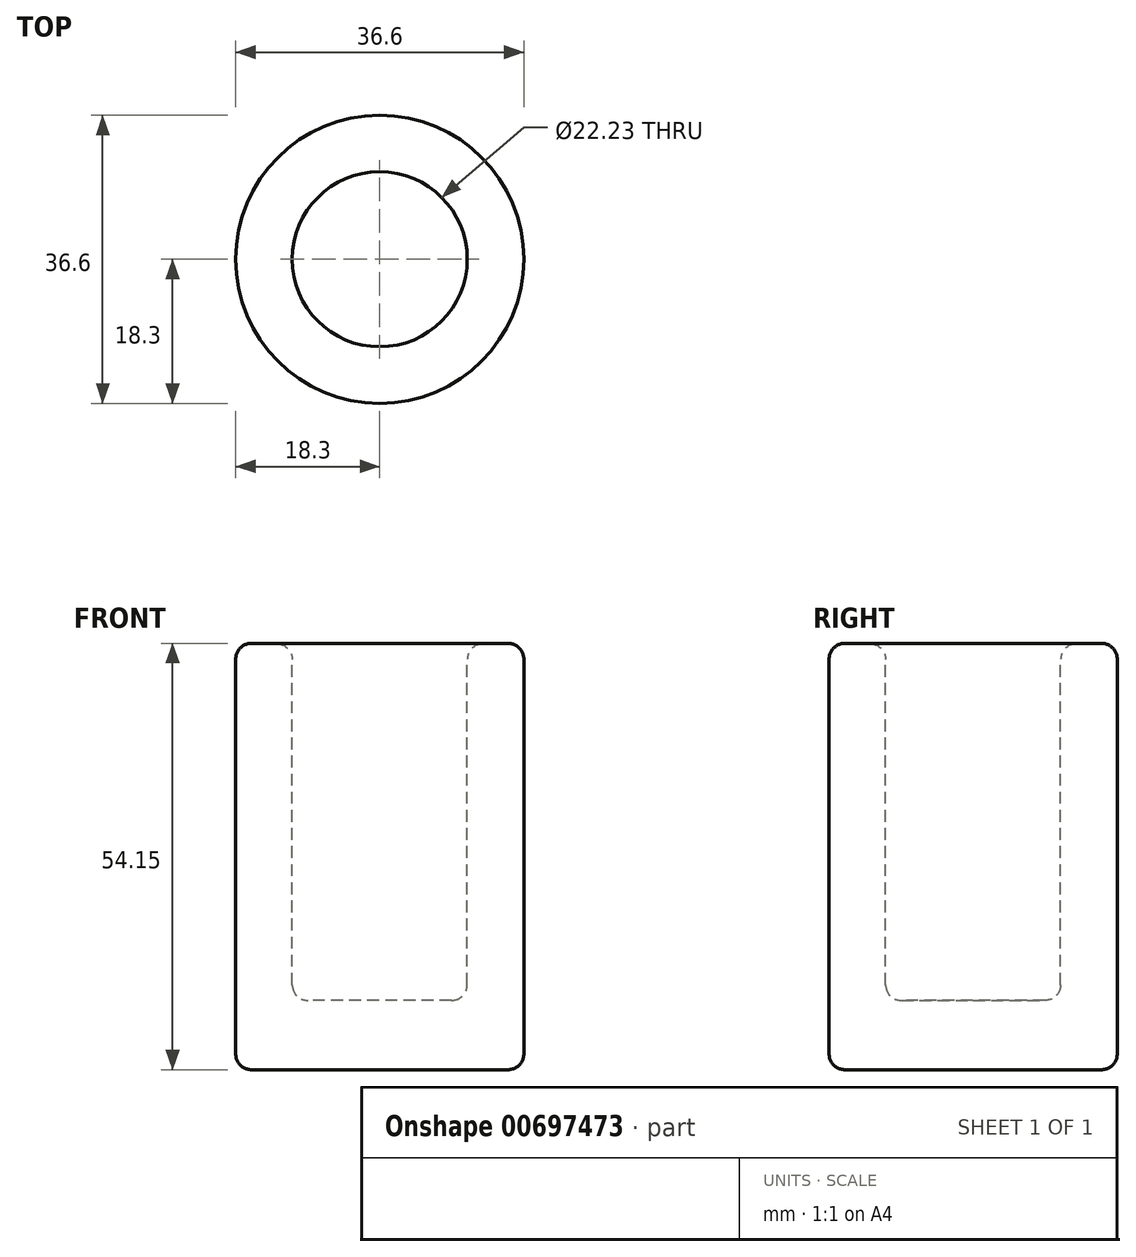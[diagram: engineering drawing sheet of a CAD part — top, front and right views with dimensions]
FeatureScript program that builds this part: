
annotation { "Feature Type Name" : "Feature", "Feature Type Description" : "" }
export const myFeature = defineFeature(function(context is Context, id is Id, definition is map)
    precondition{}
    {
        {
            var Q0;
            Q0=qCreatedBy(makeId("Front.planeOp"),FACE);
            var sketch = newSketch(context, id + "F0", { "sketchPlane" : qUnion([Q0])});
            skLineSegment(sketch, "E0", {"start": v(-18.3, 35.24) * mm, "end": v(-18.3, -14.91) * mm});
            skLineSegment(sketch, "E1", {"start": v(-16.3, -16.91) * mm, "end": v(0, -16.91) * mm});
            skLineSegment(sketch, "E2", {"start": v(0, -16.91) * mm, "end": v(0, -8.12) * mm});
            skLineSegment(sketch, "E3", {"start": v(0, -8.12) * mm, "end": v(-9.12, -8.12) * mm});
            skLineSegment(sketch, "E4", {"start": v(-11.12, -6.12) * mm, "end": v(-11.12, 35.19) * mm});
            skLineSegment(sketch, "E5", {"start": v(-13.08, 37.19) * mm, "end": v(-16.27, 37.24) * mm});
            skPoint(sketch, "E6.visualSharp", {"position": v(-18.3, 37.28) * mm});
            skArc(sketch, "E6.filletArc", {"start": v(-16.27, 37.24) * mm, "mid": v(-17.7, 36.67) * mm, "end": v(-18.3, 35.24) * mm});
            skPoint(sketch, "E7.visualSharp", {"position": v(-11.12, 37.16) * mm});
            skArc(sketch, "E7.filletArc", {"start": v(-11.12, 35.19) * mm, "mid": v(-11.7, 36.6) * mm, "end": v(-13.08, 37.19) * mm});
            skPoint(sketch, "E8.visualSharp", {"position": v(-18.3, -16.91) * mm});
            skArc(sketch, "E8.filletArc", {"start": v(-18.3, -14.91) * mm, "mid": v(-17.71, -16.33) * mm, "end": v(-16.3, -16.91) * mm});
            skPoint(sketch, "E9.visualSharp", {"position": v(-11.12, -8.12) * mm});
            skArc(sketch, "E9.filletArc", {"start": v(-11.12, -6.12) * mm, "mid": v(-10.53, -7.53) * mm, "end": v(-9.12, -8.12) * mm});
            skLineSegment(sketch, "E10", {"start": v(0, 66) * mm, "end": v(0, -44.42) * mm, "construction": true});
            skSolve(sketch);
        }
        {
            var Q0;
            Q0 = qSketchRegion(id + "F0", true);
            var Q1;
            Q1=sQuery(id+"F0.wireOp",EDGE,"E10");
            revolve(context, id + "F1", {"entities" : qUnion([Q0]), "axis" : qUnion([Q1]), "revolveType" : RevolveType.FULL});
        }
    });
